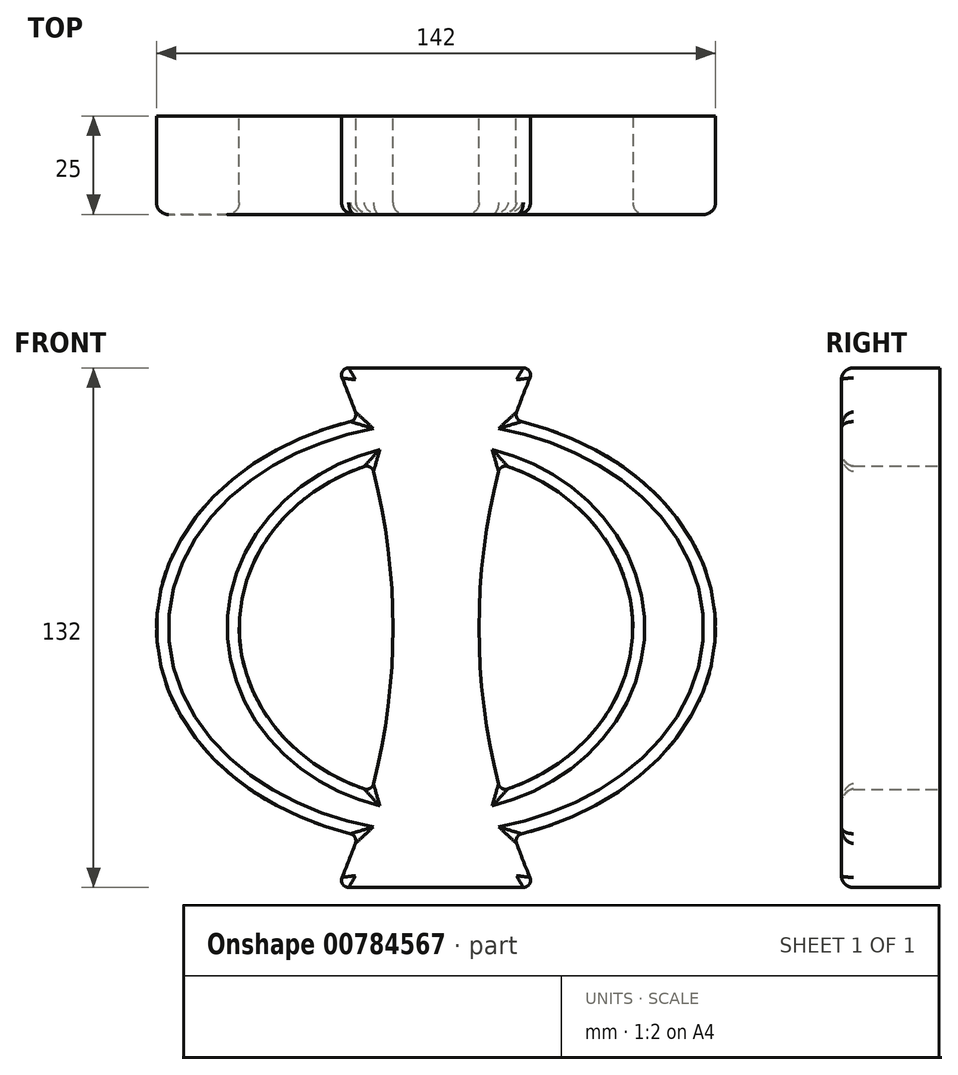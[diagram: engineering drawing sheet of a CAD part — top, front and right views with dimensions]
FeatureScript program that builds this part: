
annotation { "Feature Type Name" : "Feature", "Feature Type Description" : "" }
export const myFeature = defineFeature(function(context is Context, id is Id, definition is map)
    precondition{}
    {
        {
            var Q0;
            Q0=qCreatedBy(makeId("Front.planeOp"),FACE);
            var sketch = newSketch(context, id + "F0", { "sketchPlane" : qUnion([Q0])});
            skEllipse(sketch, "E0", {"center": v(0, 0) * mm, "majorRadius": 71 * mm, "minorRadius": 55 * mm, "majorAxis": v(1, 0)});
            skArc(sketch, "E1", {"start": v(-25, -66) * mm, "mid": v(-10.93, 0) * mm, "end": v(-25, 66) * mm});
            skLineSegment(sketch, "E2", {"start": v(0, 13.12) * mm, "end": v(0, -14.08) * mm, "construction": true});
            skArc(sketch, "E3.MirrorCS", {"start": v(25, -66) * mm, "mid": v(10.93, 0) * mm, "end": v(25, 66) * mm});
            skLineSegment(sketch, "E4", {"start": v(-25, -66) * mm, "end": v(25, -66) * mm});
            skLineSegment(sketch, "E5", {"start": v(25, 66) * mm, "end": v(-25, 66) * mm});
            skEllipse(sketch, "E6", {"center": v(0, 0) * mm, "majorRadius": 50 * mm, "minorRadius": 44 * mm, "majorAxis": v(1, 0)});
            skSolve(sketch);
        }
        {
            var Q0;
            Q0 = qSketchRegion(id + "F0", true);
            var Q1;
            {var subQ0=sQuery(id+"F0.wireOp",EDGE,"E1");var subQ1=sQuery(id+"F0.wireOp",EDGE,"XCKnHQp8-sN0c-tPIw-JVkW-WPBXkmxhwVvL");var subQ2=makeQuery(id+"F0.imprint","INTERSECT",VERTEX,{"disambiguationData":[OD(0.0)],"derivedFrom":[subQ1,subQ0]});Q1=makeQuery(id+"F0.imprint","IMPRINT",FACE,{"disambiguationData":[TD([[makeQuery(id+"F0.imprint","IMPRINT",EDGE,{"disambiguationData":[TD([[subQ2,1.0]])],"derivedFrom":subQ1}),1.0]])]});}
            var Q2;
            {var subQ0=sQuery(id+"F0.wireOp",EDGE,"E6");var subQ1=sQuery(id+"F0.wireOp",EDGE,"E1");var subQ2=makeQuery(id+"F0.imprint","INTERSECT",VERTEX,{"disambiguationData":[OD(0.0)],"derivedFrom":[subQ1,subQ0]});Q2=makeQuery(id+"F0.imprint","IMPRINT",FACE,{"disambiguationData":[TD([[makeQuery(id+"F0.imprint","IMPRINT",EDGE,{"disambiguationData":[TD([[subQ2,-1.0]])],"derivedFrom":subQ1}),-1.0]])]});}
            extrude(context, id + "F1", {"entities" : qUnion([Q0, Q1, Q2]), "depth" : 25 * mm, "offsetDistance" : 25 * mm});
        }
        {
            var Q0;
            Q0=makeQuery(id+"F1.opExtrude","CAP_FACE",FACE,{"disambiguationData":[OSD([sQuery(id+"F0.wireOp",EDGE,"E0"),sQuery(id+"F0.wireOp",EDGE,"E1"),sQuery(id+"F0.wireOp",EDGE,"E3.MirrorCS"),sQuery(id+"F0.wireOp",EDGE,"E4"),sQuery(id+"F0.wireOp",EDGE,"E5"),sQuery(id+"F0.wireOp",EDGE,"E6")])],"isStart":false});
            fillet(context, id + "F2", {"entities" : qUnion([Q0]), "radius" : 3 * mm, "tangentPropagation" : true, "allowEdgeOverflow" : false});
        }
        {
            var Q0;
            Q0=makeQuery(id+"F1.opExtrude","SWEPT_EDGE",EDGE,{"disambiguationData":[OSD([sQuery(id+"F0.wireOp",EDGE,"E1"),sQuery(id+"F0.wireOp",EDGE,"E5")])]});
            var Q1;
            {var subQ0=sQuery(id+"F0.wireOp",EDGE,"E1");var subQ1=sQuery(id+"F0.wireOp",EDGE,"E0");Q1=makeQuery(id+"F1.opExtrude","SWEPT_EDGE",EDGE,{"disambiguationData":[OSD([subQ1,subQ0]),TDD([makeQuery(id+"F0.imprint","INTERSECT",VERTEX,{"disambiguationData":[OD(0.0)],"derivedFrom":[subQ1,subQ0]})])]});}
            var Q2;
            {var subQ0=sQuery(id+"F0.wireOp",EDGE,"E6");var subQ1=sQuery(id+"F0.wireOp",EDGE,"E1");Q2=makeQuery(id+"F1.opExtrude","SWEPT_EDGE",EDGE,{"disambiguationData":[OSD([subQ1,subQ0]),TDD([makeQuery(id+"F0.imprint","INTERSECT",VERTEX,{"disambiguationData":[OD(1.0)],"derivedFrom":[subQ1,subQ0]})])]});}
            var Q3;
            {var subQ0=sQuery(id+"F0.wireOp",EDGE,"E6");var subQ1=sQuery(id+"F0.wireOp",EDGE,"E1");Q3=makeQuery(id+"F1.opExtrude","SWEPT_EDGE",EDGE,{"disambiguationData":[OSD([subQ1,subQ0]),TDD([makeQuery(id+"F0.imprint","INTERSECT",VERTEX,{"disambiguationData":[OD(0.0)],"derivedFrom":[subQ1,subQ0]})])]});}
            var Q4;
            {var subQ0=sQuery(id+"F0.wireOp",EDGE,"E1");var subQ1=sQuery(id+"F0.wireOp",EDGE,"E0");Q4=makeQuery(id+"F1.opExtrude","SWEPT_EDGE",EDGE,{"disambiguationData":[OSD([subQ1,subQ0]),TDD([makeQuery(id+"F0.imprint","INTERSECT",VERTEX,{"disambiguationData":[OD(1.0)],"derivedFrom":[subQ1,subQ0]})])]});}
            var Q5;
            Q5=makeQuery(id+"F1.opExtrude","SWEPT_EDGE",EDGE,{"disambiguationData":[OSD([sQuery(id+"F0.wireOp",EDGE,"E1"),sQuery(id+"F0.wireOp",EDGE,"E4")])]});
            var Q6;
            Q6=makeQuery(id+"F1.opExtrude","SWEPT_EDGE",EDGE,{"disambiguationData":[OSD([sQuery(id+"F0.wireOp",EDGE,"E3.MirrorCS"),sQuery(id+"F0.wireOp",EDGE,"E4")])]});
            var Q7;
            {var subQ0=sQuery(id+"F0.wireOp",EDGE,"E3.MirrorCS");var subQ1=sQuery(id+"F0.wireOp",EDGE,"E0");Q7=makeQuery(id+"F1.opExtrude","SWEPT_EDGE",EDGE,{"disambiguationData":[OSD([subQ1,subQ0]),TDD([makeQuery(id+"F0.imprint","INTERSECT",VERTEX,{"disambiguationData":[OD(1.0)],"derivedFrom":[subQ1,subQ0]})])]});}
            var Q8;
            {var subQ0=sQuery(id+"F0.wireOp",EDGE,"E6");var subQ1=sQuery(id+"F0.wireOp",EDGE,"E3.MirrorCS");Q8=makeQuery(id+"F1.opExtrude","SWEPT_EDGE",EDGE,{"disambiguationData":[OSD([subQ1,subQ0]),TDD([makeQuery(id+"F0.imprint","INTERSECT",VERTEX,{"disambiguationData":[OD(0.0)],"derivedFrom":[subQ1,subQ0]})])]});}
            var Q9;
            {var subQ0=sQuery(id+"F0.wireOp",EDGE,"E6");var subQ1=sQuery(id+"F0.wireOp",EDGE,"E3.MirrorCS");Q9=makeQuery(id+"F1.opExtrude","SWEPT_EDGE",EDGE,{"disambiguationData":[OSD([subQ1,subQ0]),TDD([makeQuery(id+"F0.imprint","INTERSECT",VERTEX,{"disambiguationData":[OD(1.0)],"derivedFrom":[subQ1,subQ0]})])]});}
            var Q10;
            {var subQ0=sQuery(id+"F0.wireOp",EDGE,"E3.MirrorCS");var subQ1=sQuery(id+"F0.wireOp",EDGE,"E0");Q10=makeQuery(id+"F1.opExtrude","SWEPT_EDGE",EDGE,{"disambiguationData":[OSD([subQ1,subQ0]),TDD([makeQuery(id+"F0.imprint","INTERSECT",VERTEX,{"disambiguationData":[OD(0.0)],"derivedFrom":[subQ1,subQ0]})])]});}
            var Q11;
            Q11=makeQuery(id+"F1.opExtrude","SWEPT_EDGE",EDGE,{"disambiguationData":[OSD([sQuery(id+"F0.wireOp",EDGE,"E3.MirrorCS"),sQuery(id+"F0.wireOp",EDGE,"E5")])]});
            fillet(context, id + "F3", {"entities" : qUnion([Q0, Q1, Q2, Q3, Q4, Q5, Q6, Q7, Q8, Q9, Q10, Q11]), "radius" : 1.85 * mm, "tangentPropagation" : true, "allowEdgeOverflow" : false});
        }
    });
